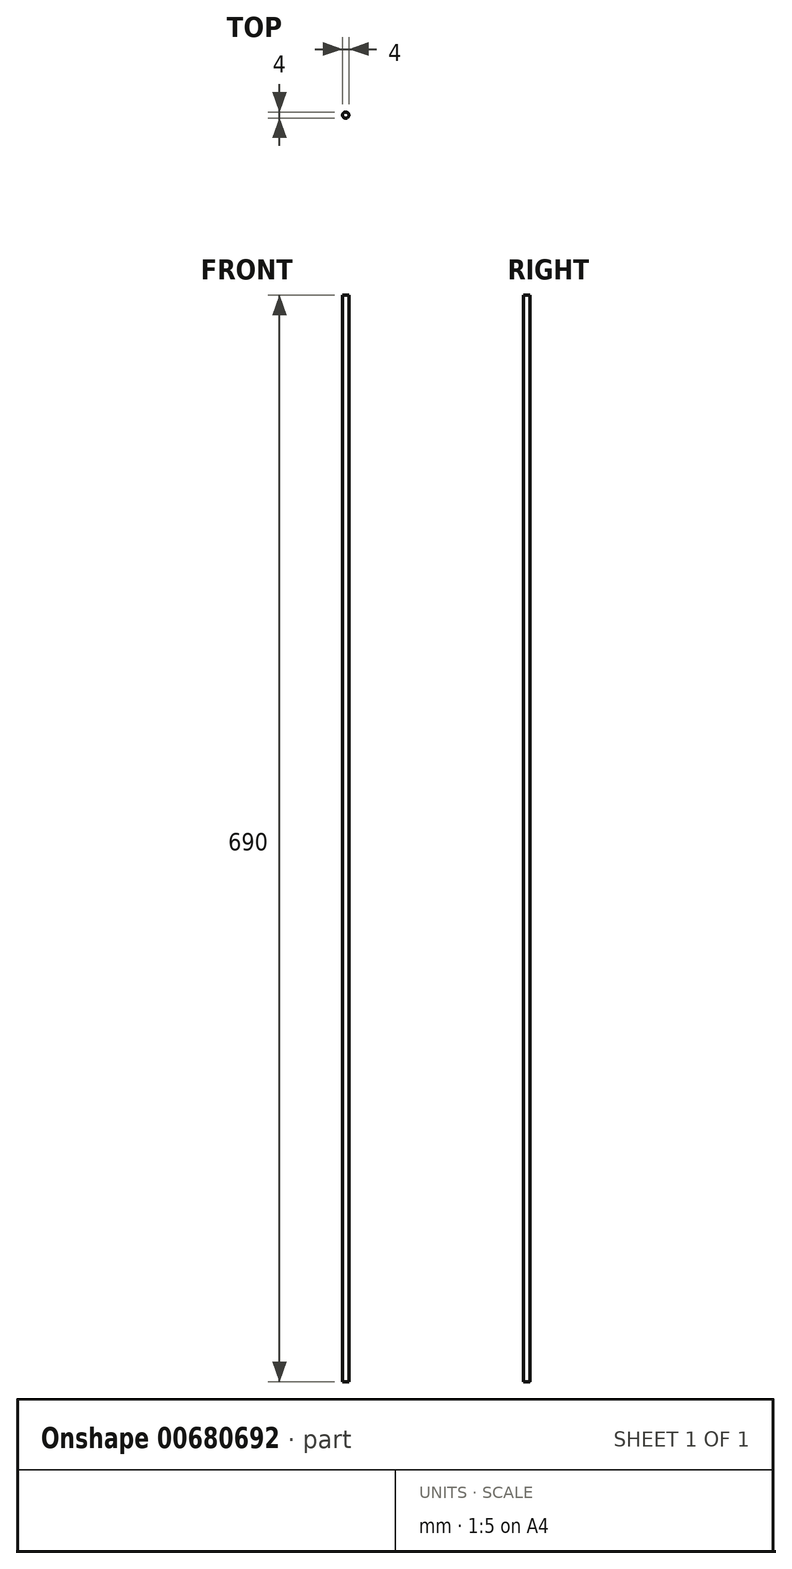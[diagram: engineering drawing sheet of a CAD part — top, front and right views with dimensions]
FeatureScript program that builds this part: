
annotation { "Feature Type Name" : "Feature", "Feature Type Description" : "" }
export const myFeature = defineFeature(function(context is Context, id is Id, definition is map)
    precondition{}
    {
        {
            var Q0;
            Q0=qCreatedBy(makeId("Top.planeOp"),FACE);
            var sketch = newSketch(context, id + "F0", { "sketchPlane" : qUnion([Q0])});
            skCircle(sketch, "E0", {"center": v(0, 0) * mm, "radius": 2 * mm});
            skSolve(sketch);
        }
        {
            var Q0;
            Q0=makeQuery(id+"F0.imprint","IMPRINT",FACE,{"disambiguationData":[TD([[makeQuery(id+"F0.imprint","IMPRINT",EDGE,{"derivedFrom":sQuery(id+"F0.wireOp",EDGE,"E0")}),1.0]])]});
            extrude(context, id + "F1", {"entities" : qUnion([Q0]), "depth" : 690 * mm, "offsetDistance" : 25 * mm});
        }
    });
